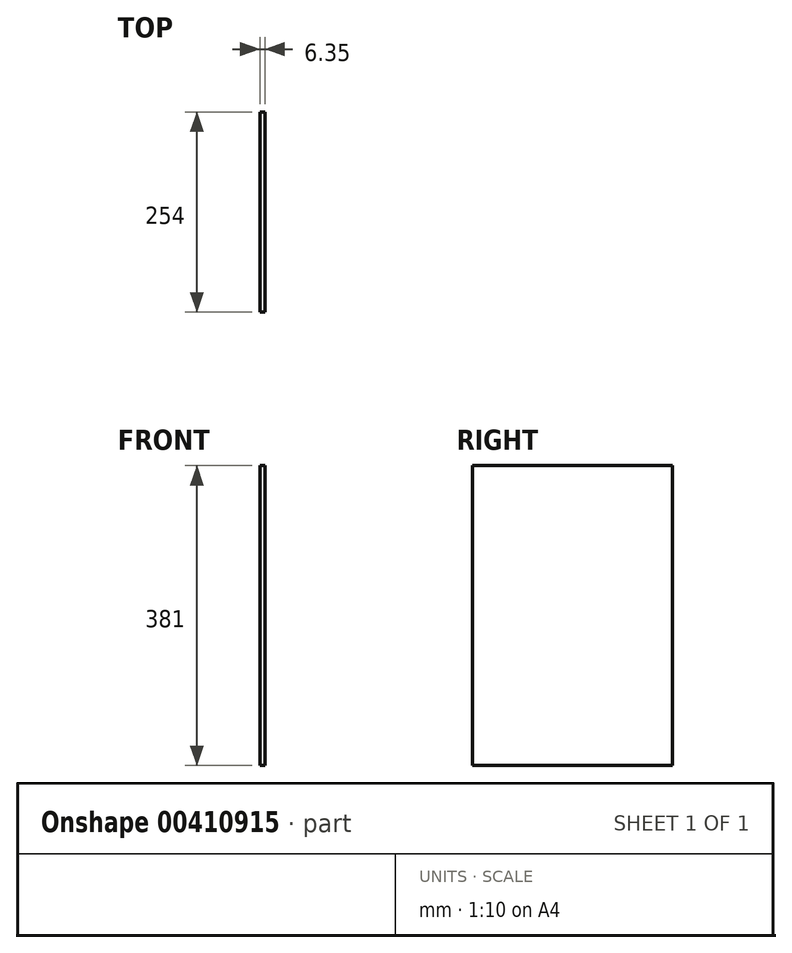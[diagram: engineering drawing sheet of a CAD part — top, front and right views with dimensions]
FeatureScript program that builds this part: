
annotation { "Feature Type Name" : "Feature", "Feature Type Description" : "" }
export const myFeature = defineFeature(function(context is Context, id is Id, definition is map)
    precondition{}
    {
        {
            var Q0;
            Q0=qCreatedBy(makeId("Right.planeOp"),FACE);
            var sketch = newSketch(context, id + "F0", { "sketchPlane" : qUnion([Q0])});
            skLineSegment(sketch, "E0", {"start": v(0, 0) * mm, "end": v(0, 381) * mm});
            skLineSegment(sketch, "E1", {"start": v(0, 381) * mm, "end": v(254, 381) * mm});
            skLineSegment(sketch, "E2", {"start": v(254, 381) * mm, "end": v(254, 0) * mm});
            skLineSegment(sketch, "E3", {"start": v(254, 0) * mm, "end": v(0, 0) * mm});
            skSolve(sketch);
        }
        {
            var Q0;
            Q0 = qSketchRegion(id + "F0", true);
            extrude(context, id + "F1", {"entities" : qUnion([Q0]), "depth" : 6.35 * mm});
        }
    });
